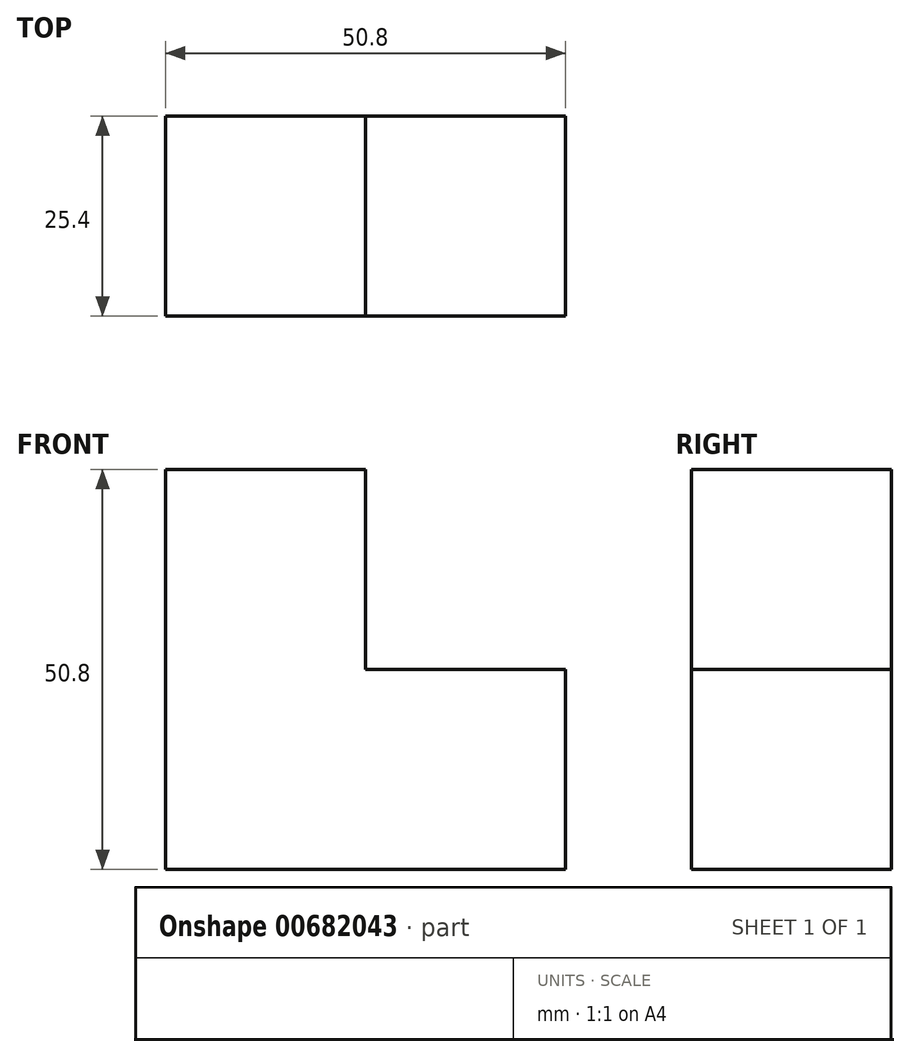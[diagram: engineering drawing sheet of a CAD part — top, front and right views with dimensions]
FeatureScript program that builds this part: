
annotation { "Feature Type Name" : "Feature", "Feature Type Description" : "" }
export const myFeature = defineFeature(function(context is Context, id is Id, definition is map)
    precondition{}
    {
        {
            var Q0;
            Q0=qCreatedBy(makeId("Front.planeOp"),FACE);
            var sketch = newSketch(context, id + "F0", { "sketchPlane" : qUnion([Q0])});
            skLineSegment(sketch, "E0", {"start": v(0, 0) * mm, "end": v(-50.8, 0) * mm});
            skLineSegment(sketch, "E1", {"start": v(-50.8, 0) * mm, "end": v(-50.8, 50.8) * mm});
            skLineSegment(sketch, "E2", {"start": v(-50.8, 50.8) * mm, "end": v(-25.4, 50.8) * mm});
            skLineSegment(sketch, "E3", {"start": v(-25.4, 50.8) * mm, "end": v(-25.4, 25.4) * mm});
            skLineSegment(sketch, "E4", {"start": v(-25.4, 25.4) * mm, "end": v(0, 25.4) * mm});
            skLineSegment(sketch, "E5", {"start": v(0, 0) * mm, "end": v(0, 25.4) * mm});
            skSolve(sketch);
        }
        {
            var Q0;
            Q0 = qSketchRegion(id + "F0", true);
            extrude(context, id + "F1", {"entities" : qUnion([Q0]), "depth" : 25.4 * mm, "offsetDistance" : 25.4 * mm});
        }
    });
